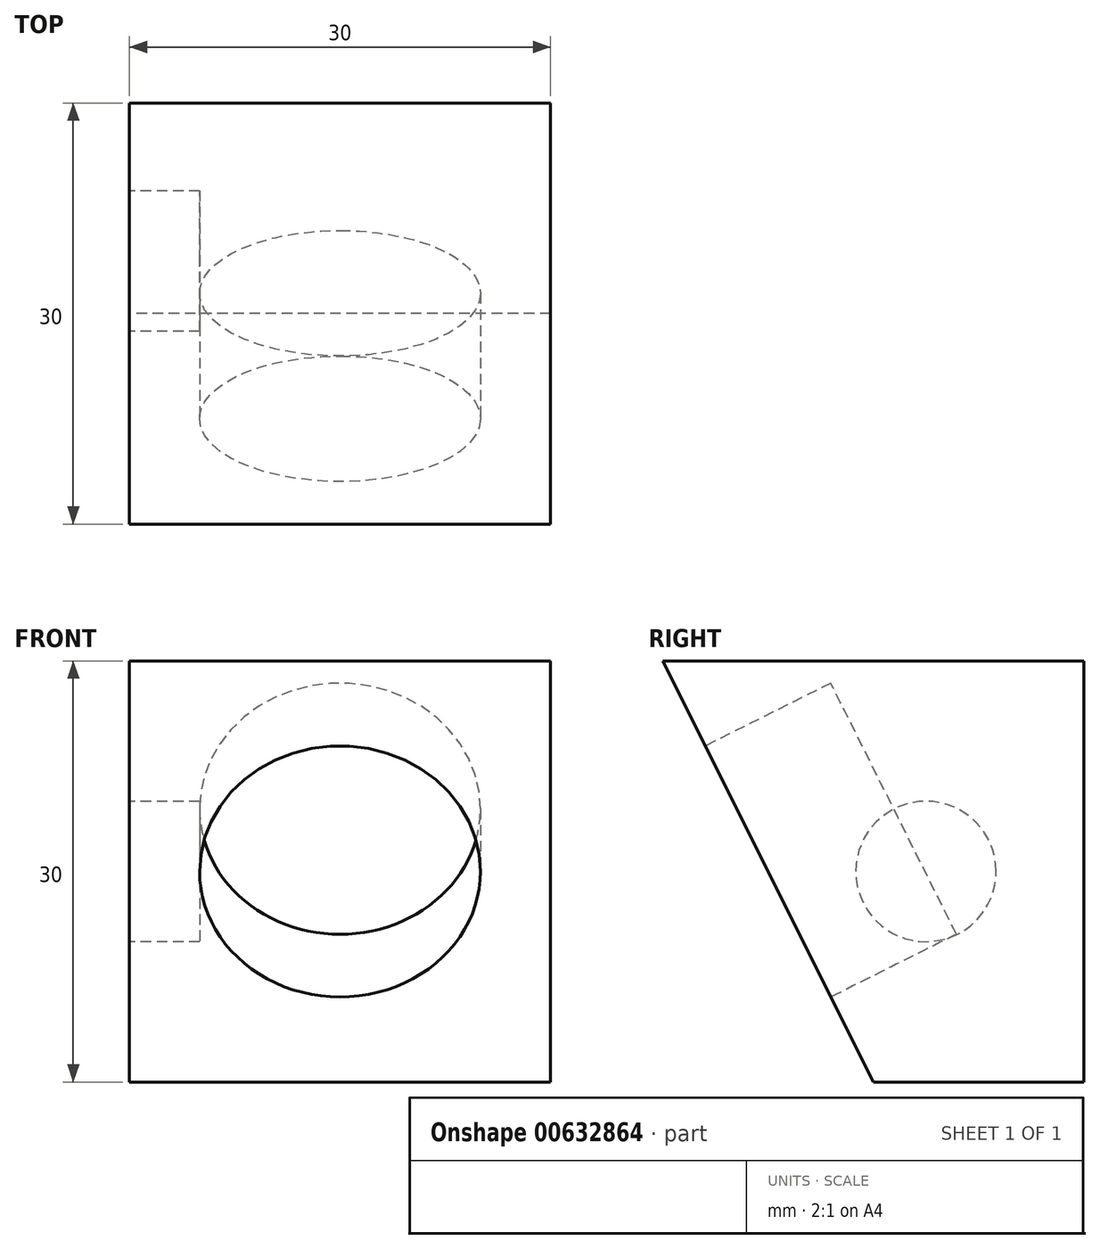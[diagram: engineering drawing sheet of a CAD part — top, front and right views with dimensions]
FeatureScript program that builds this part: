
annotation { "Feature Type Name" : "Feature", "Feature Type Description" : "" }
export const myFeature = defineFeature(function(context is Context, id is Id, definition is map)
    precondition{}
    {
        {
            var Q0;
            Q0=qCreatedBy(makeId("Front.planeOp"),FACE);
            var sketch = newSketch(context, id + "F0", { "sketchPlane" : qUnion([Q0])});
            skLineSegment(sketch, "E0.bottom", {"start": v(15, 15) * mm, "end": v(-15, 15) * mm});
            skLineSegment(sketch, "E0.top", {"start": v(15, -15) * mm, "end": v(-15, -15) * mm});
            skLineSegment(sketch, "E0.left", {"start": v(15, 15) * mm, "end": v(15, -15) * mm});
            skLineSegment(sketch, "E0.right", {"start": v(-15, 15) * mm, "end": v(-15, -15) * mm});
            skPoint(sketch, "E0.middle", {"position": v(0, 0) * mm});
            skSolve(sketch);
        }
        {
            var Q0;
            Q0=makeQuery(id+"F0.imprint","IMPRINT",FACE,{"disambiguationData":[TD([[makeQuery(id+"F0.imprint","IMPRINT",EDGE,{"derivedFrom":sQuery(id+"F0.wireOp",EDGE,"E0.bottom")}),1.0]])]});
            extrude(context, id + "F1", {"entities" : qUnion([Q0]), "depth" : 30 * mm, "offsetDistance" : 25.4 * mm});
        }
        {
            var Q0;
            Q0=makeQuery(id+"F1.opExtrude","SWEPT_FACE",FACE,{"disambiguationData":[OSD([sQuery(id+"F0.wireOp",EDGE,"E0.right")])]});
            var sketch = newSketch(context, id + "F2", { "sketchPlane" : qUnion([Q0])});
            skLineSegment(sketch, "E1", {"start": v(30, 15) * mm, "end": v(15, -15) * mm});
            skSolve(sketch);
        }
        {
            var Q0;
            {var subQ0=sQuery(id+"F2.wireOp",EDGE,"E1");Q0=makeQuery(id+"F2.imprint","IMPRINT",FACE,{"disambiguationData":[TD([[makeQuery(id+"F2.imprint","IMPRINT",EDGE,{"derivedFrom":subQ0}),1.0]])]});}
            extrude(context, id + "F3", {"entities" : qUnion([Q0]), "operationType" : NewBodyOperationType.REMOVE, "oppositeDirection" : true, "depth" : 30 * mm, "offsetDistance" : 25.4 * mm});
        }
        {
            var Q0;
            Q0=makeQuery(id+"F3.boolean.opBoolean","COPY",FACE,{"derivedFrom":makeQuery(id+"F3.opExtrude","SWEPT_FACE",FACE,{"disambiguationData":[OSD([sQuery(id+"F2.wireOp",EDGE,"E1")])]})});
            var sketch = newSketch(context, id + "F4", { "sketchPlane" : qUnion([Q0])});
            skLineSegment(sketch, "E2", {"start": v(-15, 10.06) * mm, "end": v(15, 10.06) * mm, "construction": true});
            skLineSegment(sketch, "E3.bottom", {"start": v(10, 20.06) * mm, "end": v(-10, 20.06) * mm, "construction": true});
            skLineSegment(sketch, "E3.top", {"start": v(10, 0.06) * mm, "end": v(-10, 0.06) * mm, "construction": true});
            skLineSegment(sketch, "E3.left", {"start": v(10, 20.06) * mm, "end": v(10, 0.06) * mm, "construction": true});
            skLineSegment(sketch, "E3.right", {"start": v(-10, 20.06) * mm, "end": v(-10, 0.06) * mm, "construction": true});
            skPoint(sketch, "E3.middle", {"position": v(0, 10.06) * mm});
            skCircle(sketch, "E4", {"center": v(0, 10.06) * mm, "radius": 10 * mm});
            skSolve(sketch);
        }
        {
            var Q0;
            Q0=makeQuery(id+"F4.imprint","IMPRINT",FACE,{"disambiguationData":[TD([[makeQuery(id+"F4.imprint","IMPRINT",EDGE,{"derivedFrom":sQuery(id+"F4.wireOp",EDGE,"E4")}),1.0]])]});
            extrude(context, id + "F5", {"entities" : qUnion([Q0]), "operationType" : NewBodyOperationType.REMOVE, "oppositeDirection" : true, "depth" : 10 * mm, "offsetDistance" : 25.4 * mm});
        }
        {
            var Q0;
            Q0=makeQuery(id+"F1.opExtrude","SWEPT_FACE",FACE,{"disambiguationData":[OSD([sQuery(id+"F0.wireOp",EDGE,"E0.right")])]});
            var sketch = newSketch(context, id + "F6", { "sketchPlane" : qUnion([Q0])});
            skLineSegment(sketch, "E5", {"start": v(22.5, 0) * mm, "end": v(0, 0) * mm, "construction": true});
            skCircle(sketch, "E6", {"center": v(11.25, 0) * mm, "radius": 5 * mm});
            skSolve(sketch);
        }
        {
            var Q0;
            Q0=makeQuery(id+"F6.imprint","IMPRINT",FACE,{"disambiguationData":[TD([[makeQuery(id+"F6.imprint","IMPRINT",EDGE,{"derivedFrom":sQuery(id+"F6.wireOp",EDGE,"E6")}),1.0]])]});
            extrude(context, id + "F7", {"entities" : qUnion([Q0]), "operationType" : NewBodyOperationType.REMOVE, "oppositeDirection" : true, "depth" : 5 * mm, "offsetDistance" : 25.4 * mm});
        }
    });
